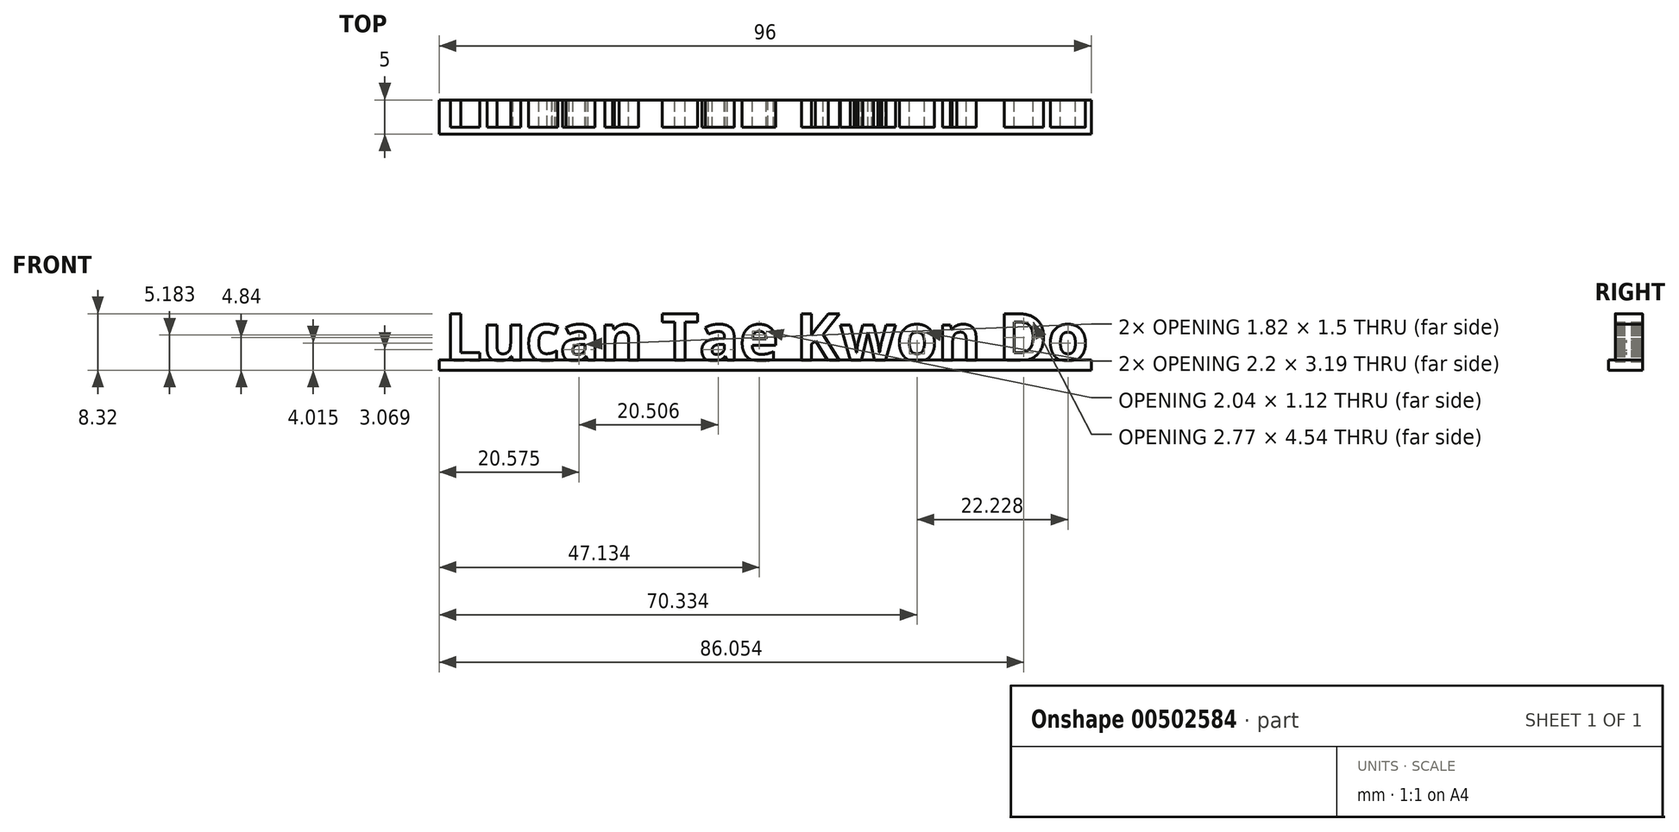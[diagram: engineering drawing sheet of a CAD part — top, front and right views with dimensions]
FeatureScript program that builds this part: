
annotation { "Feature Type Name" : "Feature", "Feature Type Description" : "" }
export const myFeature = defineFeature(function(context is Context, id is Id, definition is map)
    precondition{}
    {
        {
            var Q0;
            Q0=qCreatedBy(makeId("Front.planeOp"),FACE);
            var sketch = newSketch(context, id + "F0", { "sketchPlane" : qUnion([Q0])});
            skText(sketch, "E0", { "text": "Lucan Tae Kwon Do ", "fontName": "OpenSans-Bold.ttf"});
            const initialGuessF0  = {"E0": [-0.03534, 0.00742, 1, 0, 0.00703]};
            skSetInitialGuess(sketch, initialGuessF0);
            skSolve(sketch);
        }
        {
            var Q0;
            Q0 = qSketchRegion(id + "F0", true);
            extrude(context, id + "F1", {"entities" : qUnion([Q0]), "depth" : 4 * mm, "offsetDistance" : 25 * mm});
        }
        {
            var Q0;
            Q0=qCreatedBy(makeId("Front.planeOp"),FACE);
            var sketch = newSketch(context, id + "F2", { "sketchPlane" : qUnion([Q0])});
            skLineSegment(sketch, "E1.bottom", {"start": v(-36.15, 7.57) * mm, "end": v(59.85, 7.57) * mm});
            skLineSegment(sketch, "E1.top", {"start": v(-36.15, 6.07) * mm, "end": v(59.85, 6.07) * mm});
            skLineSegment(sketch, "E1.left", {"start": v(-36.15, 7.57) * mm, "end": v(-36.15, 6.07) * mm});
            skLineSegment(sketch, "E1.right", {"start": v(59.85, 7.57) * mm, "end": v(59.85, 6.07) * mm});
            skSolve(sketch);
        }
        {
            var Q0;
            Q0 = qSketchRegion(id + "F2", true);
            extrude(context, id + "F3", {"entities" : qUnion([Q0]), "depth" : 5 * mm, "offsetDistance" : 25 * mm});
        }
    });
